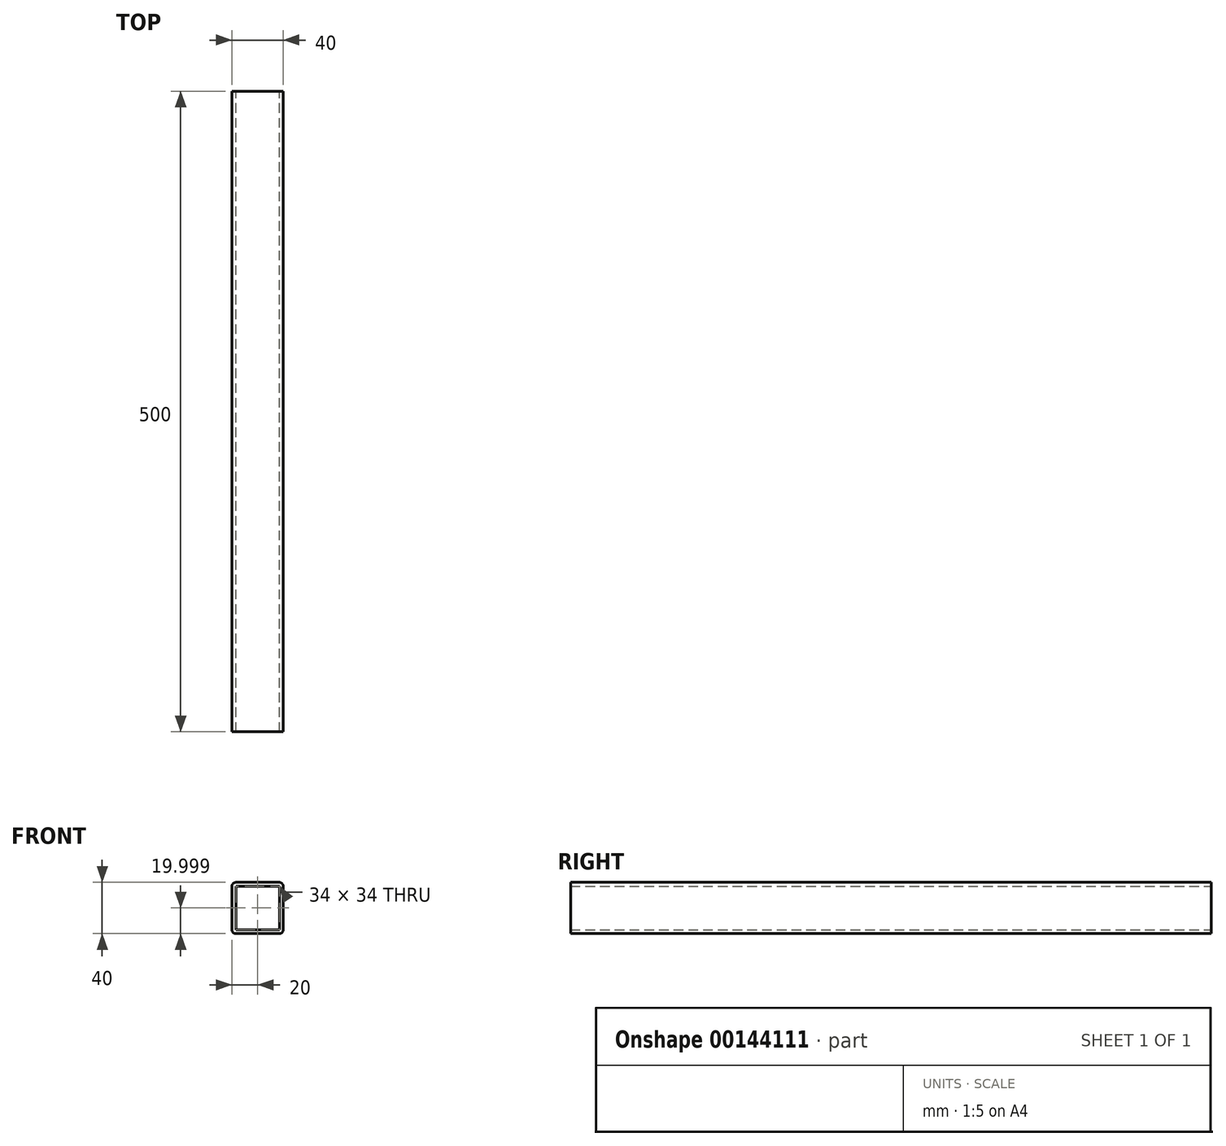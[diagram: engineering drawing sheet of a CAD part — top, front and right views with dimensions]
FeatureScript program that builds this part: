
annotation { "Feature Type Name" : "Feature", "Feature Type Description" : "" }
export const myFeature = defineFeature(function(context is Context, id is Id, definition is map)
    precondition{}
    {
        {
            var Q0;
            Q0=qCreatedBy(makeId("Front.planeOp"),FACE);
            var sketch = newSketch(context, id + "F0", { "sketchPlane" : qUnion([Q0])});
            skLineSegment(sketch, "E0.bottom", {"start": v(16.78, 20.08) * mm, "end": v(-17.22, 20.08) * mm});
            skLineSegment(sketch, "E0.top", {"start": v(16.78, -19.92) * mm, "end": v(-17.22, -19.92) * mm});
            skLineSegment(sketch, "E0.left", {"start": v(19.78, 17.08) * mm, "end": v(19.78, -16.92) * mm});
            skLineSegment(sketch, "E0.right", {"start": v(-20.22, 17.08) * mm, "end": v(-20.22, -16.92) * mm});
            skPoint(sketch, "E0.middle", {"position": v(-0.22, 0.08) * mm});
            skPoint(sketch, "E1.visualSharp", {"position": v(-20.22, 20.08) * mm});
            skArc(sketch, "E1.filletArc", {"start": v(-17.22, 20.08) * mm, "mid": v(-19.34, 19.2) * mm, "end": v(-20.22, 17.08) * mm});
            skPoint(sketch, "E2.visualSharp", {"position": v(19.78, 20.08) * mm});
            skArc(sketch, "E2.filletArc", {"start": v(19.78, 17.08) * mm, "mid": v(18.9, 19.2) * mm, "end": v(16.78, 20.08) * mm});
            skPoint(sketch, "E3.visualSharp", {"position": v(19.78, -19.92) * mm});
            skArc(sketch, "E3.filletArc", {"start": v(16.78, -19.92) * mm, "mid": v(18.9, -19.04) * mm, "end": v(19.78, -16.92) * mm});
            skPoint(sketch, "E4.visualSharp", {"position": v(-20.22, -19.92) * mm});
            skArc(sketch, "E4.filletArc", {"start": v(-20.22, -16.92) * mm, "mid": v(-19.34, -19.04) * mm, "end": v(-17.22, -19.92) * mm});
            skLineSegment(sketch, "E5.0", {"start": v(16.78, 17.08) * mm, "end": v(-17.22, 17.08) * mm});
            skLineSegment(sketch, "E5.1", {"start": v(16.78, 17.08) * mm, "end": v(16.78, -16.92) * mm});
            skLineSegment(sketch, "E5.2", {"start": v(16.78, -16.92) * mm, "end": v(-17.22, -16.92) * mm});
            skLineSegment(sketch, "E5.3", {"start": v(-17.22, 17.08) * mm, "end": v(-17.22, -16.92) * mm});
            skSolve(sketch);
        }
        {
            var Q0;
            Q0=makeQuery(id+"F0.imprint","IMPRINT",FACE,{"disambiguationData":[TD([[makeQuery(id+"F0.imprint","IMPRINT",EDGE,{"derivedFrom":sQuery(id+"F0.wireOp",EDGE,"E0.bottom")}),1.0]])]});
            extrude(context, id + "F1", {"entities" : qUnion([Q0]), "depth" : 500 * mm});
        }
    });
